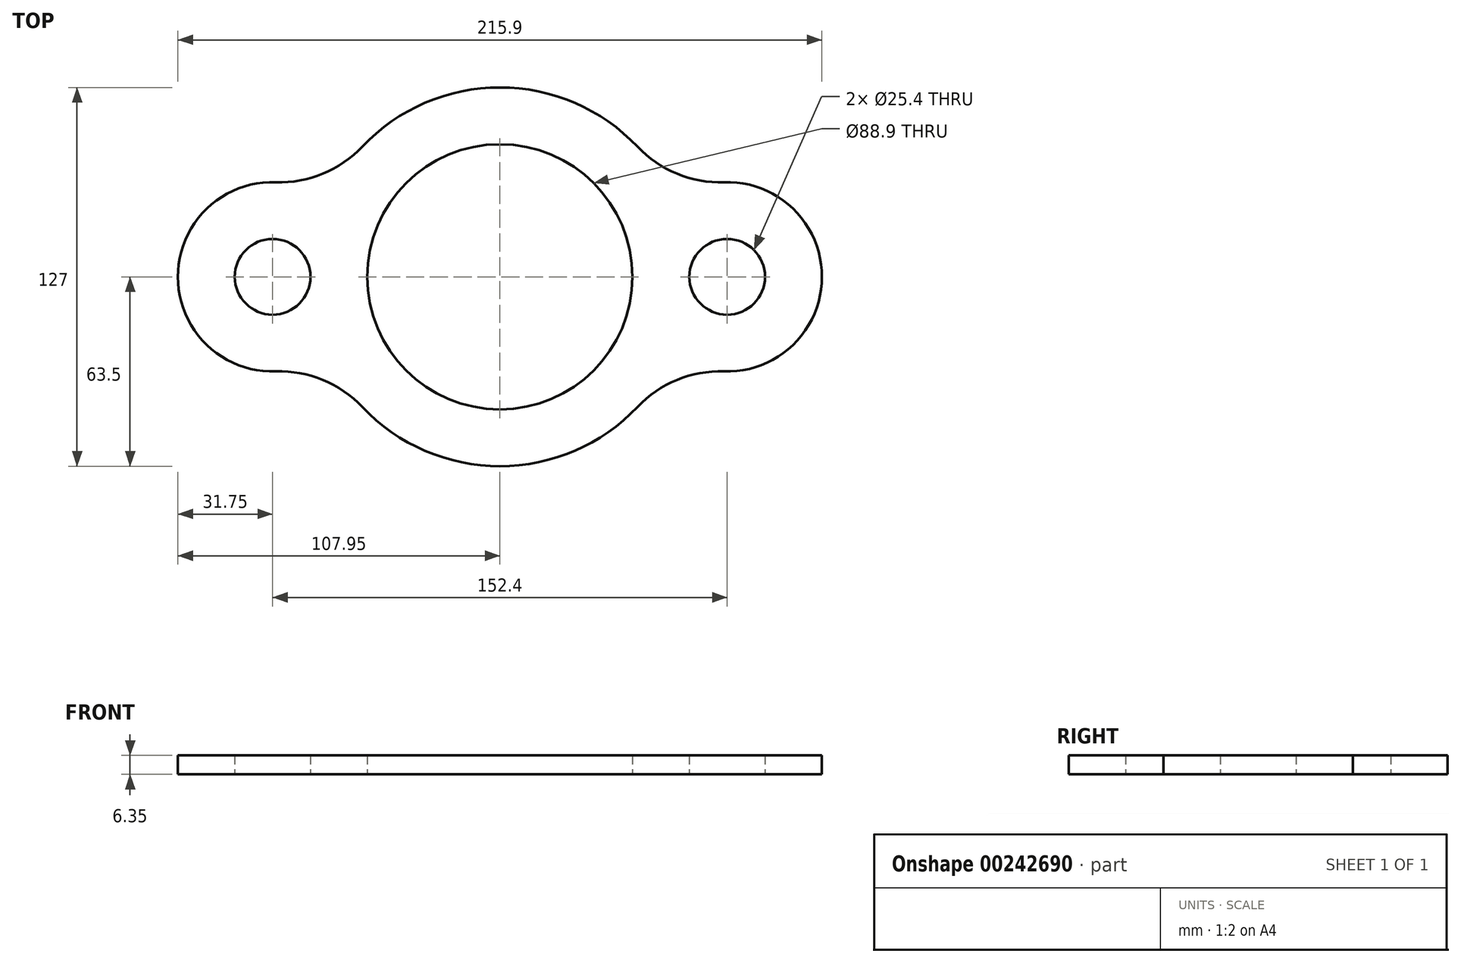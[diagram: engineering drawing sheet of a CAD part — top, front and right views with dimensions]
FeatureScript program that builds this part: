
annotation { "Feature Type Name" : "Feature", "Feature Type Description" : "" }
export const myFeature = defineFeature(function(context is Context, id is Id, definition is map)
    precondition{}
    {
        {
            var Q0;
            Q0=qCreatedBy(makeId("Top.planeOp"),FACE);
            var sketch = newSketch(context, id + "F0", { "sketchPlane" : qUnion([Q0])});
            skArc(sketch, "E0", {"start": v(-46.14, -43.63) * mm, "mid": v(0, -63.5) * mm, "end": v(46.14, -43.63) * mm});
            skCircle(sketch, "E1", {"center": v(0, 0) * mm, "radius": 44.45 * mm});
            skArc(sketch, "E2", {"start": v(75.12, -31.73) * mm, "mid": v(107.95, 0) * mm, "end": v(75.12, 31.73) * mm});
            skCircle(sketch, "E3", {"center": v(76.2, 0) * mm, "radius": 12.7 * mm});
            skArc(sketch, "E4", {"start": v(-75.12, 31.73) * mm, "mid": v(-107.95, 0) * mm, "end": v(-75.12, -31.73) * mm});
            skCircle(sketch, "E5", {"center": v(-76.2, 0) * mm, "radius": 12.7 * mm});
            skArc(sketch, "E6.trimOffspring", {"start": v(46.14, 43.63) * mm, "mid": v(0, 63.5) * mm, "end": v(-46.14, 43.63) * mm});
            skPoint(sketch, "E7.visualSharp", {"position": v(-57.94, 25.98) * mm});
            skArc(sketch, "E7.filletArc", {"start": v(-75.12, 31.73) * mm, "mid": v(-59.35, 34.56) * mm, "end": v(-46.14, 43.63) * mm});
            skPoint(sketch, "E8.visualSharp", {"position": v(57.94, 25.98) * mm});
            skArc(sketch, "E8.filletArc", {"start": v(46.14, 43.63) * mm, "mid": v(59.35, 34.56) * mm, "end": v(75.12, 31.73) * mm});
            skPoint(sketch, "E9.visualSharp", {"position": v(57.94, -25.98) * mm});
            skArc(sketch, "E9.filletArc", {"start": v(75.12, -31.73) * mm, "mid": v(59.35, -34.56) * mm, "end": v(46.14, -43.63) * mm});
            skPoint(sketch, "E10.visualSharp", {"position": v(-57.94, -25.98) * mm});
            skArc(sketch, "E10.filletArc", {"start": v(-46.14, -43.63) * mm, "mid": v(-59.35, -34.56) * mm, "end": v(-75.12, -31.73) * mm});
            skSolve(sketch);
        }
        {
            var Q0;
            Q0 = qSketchRegion(id + "F0", true);
            extrude(context, id + "F1", {"entities" : qUnion([Q0]), "depth" : 6.35 * mm});
        }
    });
